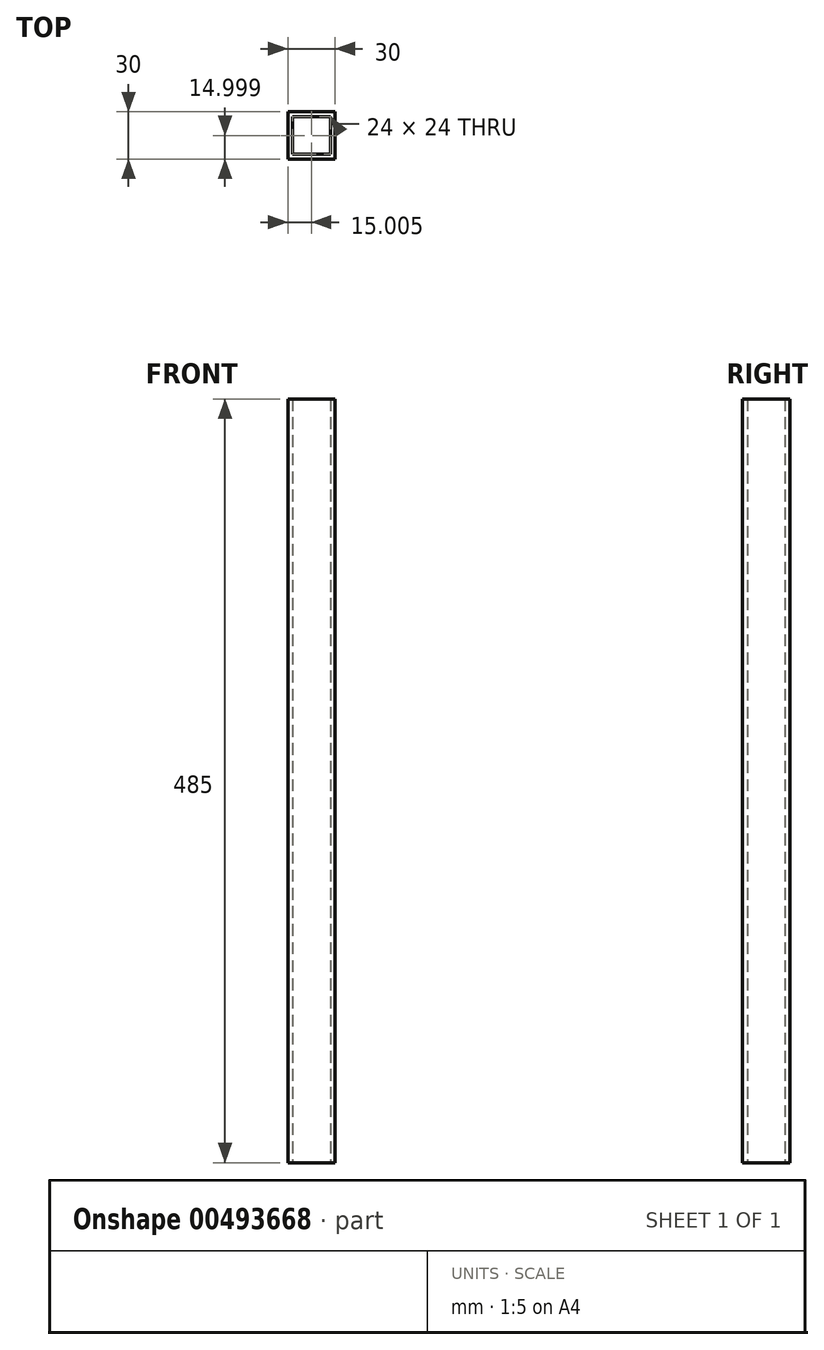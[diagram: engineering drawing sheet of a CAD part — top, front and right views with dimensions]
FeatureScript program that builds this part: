
annotation { "Feature Type Name" : "Feature", "Feature Type Description" : "" }
export const myFeature = defineFeature(function(context is Context, id is Id, definition is map)
    precondition{}
    {
        {
            var Q0;
            Q0=qCreatedBy(makeId("Top.planeOp"),FACE);
            var sketch = newSketch(context, id + "F0", { "sketchPlane" : qUnion([Q0])});
            skLineSegment(sketch, "E0.bottom", {"start": v(-9.06, 11.45) * mm, "end": v(14.94, 11.45) * mm});
            skLineSegment(sketch, "E0.top", {"start": v(-9.06, -12.55) * mm, "end": v(14.94, -12.55) * mm});
            skLineSegment(sketch, "E0.left", {"start": v(-9.06, 11.45) * mm, "end": v(-9.06, -12.55) * mm});
            skLineSegment(sketch, "E0.right", {"start": v(14.94, 11.45) * mm, "end": v(14.94, -12.55) * mm});
            skLineSegment(sketch, "E1.bottom", {"start": v(-12.06, 14.45) * mm, "end": v(17.94, 14.45) * mm});
            skLineSegment(sketch, "E1.top", {"start": v(-12.06, -15.55) * mm, "end": v(17.94, -15.55) * mm});
            skLineSegment(sketch, "E1.left", {"start": v(-12.06, 14.45) * mm, "end": v(-12.06, -15.55) * mm});
            skLineSegment(sketch, "E1.right", {"start": v(17.94, 14.45) * mm, "end": v(17.94, -15.55) * mm});
            skSolve(sketch);
        }
        {
            var Q0;
            Q0=qSketchRegion(id+"F0",true);
            extrude(context, id + "F1", {"entities" : qUnion([Q0]), "depth" : 485 * mm});
        }
    });
